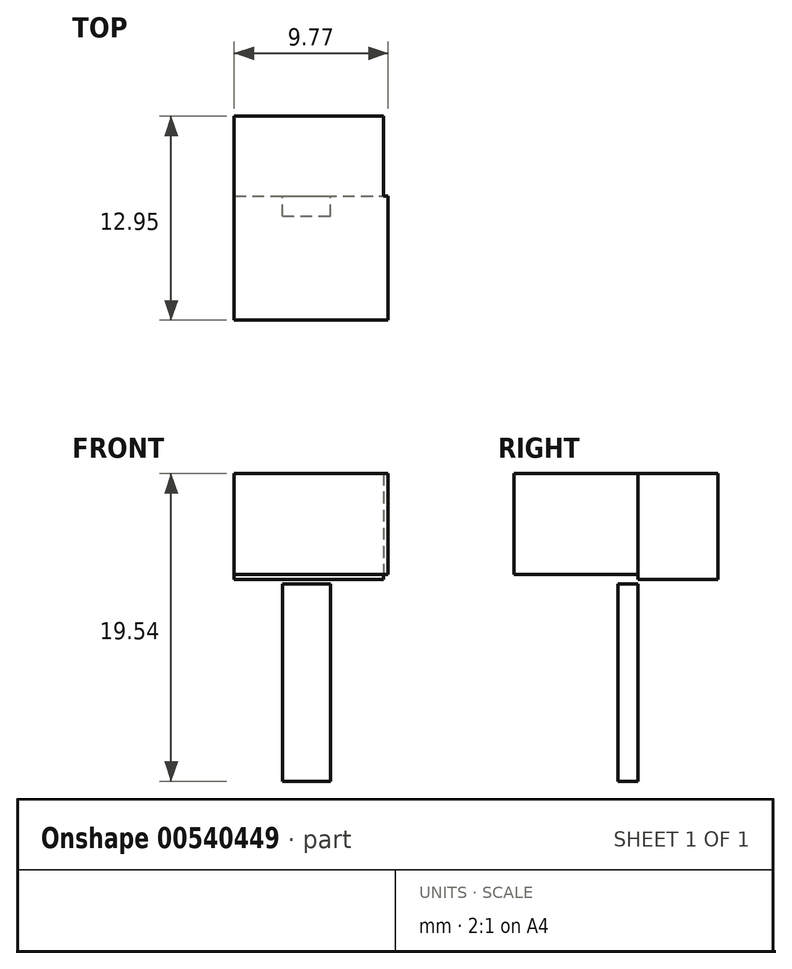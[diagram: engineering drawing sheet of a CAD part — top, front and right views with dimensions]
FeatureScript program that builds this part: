
annotation { "Feature Type Name" : "Feature", "Feature Type Description" : "" }
export const myFeature = defineFeature(function(context is Context, id is Id, definition is map)
    precondition{}
    {
        {
            var Q0;
            Q0=qCreatedBy(makeId("Front.planeOp"),FACE);
            var sketch = newSketch(context, id + "F0", { "sketchPlane" : qUnion([Q0])});
            skLineSegment(sketch, "E0.bottom", {"start": v(-57.72, -44.9) * mm, "end": v(-54.66, -44.9) * mm});
            skLineSegment(sketch, "E0.top", {"start": v(-57.72, -32.37) * mm, "end": v(-54.66, -32.37) * mm});
            skLineSegment(sketch, "E0.left", {"start": v(-57.72, -44.9) * mm, "end": v(-57.72, -32.37) * mm});
            skLineSegment(sketch, "E0.right", {"start": v(-54.66, -44.9) * mm, "end": v(-54.66, -32.37) * mm});
            skSolve(sketch);
        }
        {
            var Q0;
            Q0 = qSketchRegion(id + "F0", true);
            extrude(context, id + "F1", {"entities" : qUnion([Q0]), "depth" : 1.27 * mm, "offsetDistance" : 25.4 * mm});
        }
        {
            var Q0;
            Q0=qCreatedBy(makeId("Front.planeOp"),FACE);
            var sketch = newSketch(context, id + "F2", { "sketchPlane" : qUnion([Q0])});
            skLineSegment(sketch, "E1.bottom", {"start": v(-60.77, -31.76) * mm, "end": v(-51, -31.76) * mm});
            skLineSegment(sketch, "E1.top", {"start": v(-60.77, -25.35) * mm, "end": v(-51, -25.35) * mm});
            skLineSegment(sketch, "E1.left", {"start": v(-60.77, -31.76) * mm, "end": v(-60.77, -25.35) * mm});
            skLineSegment(sketch, "E1.right", {"start": v(-51, -31.76) * mm, "end": v(-51, -25.35) * mm});
            skSolve(sketch);
        }
        {
            var Q0;
            Q0 = qSketchRegion(id + "F2", true);
            extrude(context, id + "F3", {"entities" : qUnion([Q0]), "depth" : 7.87 * mm, "offsetDistance" : 25.4 * mm});
        }
        {
            var Q0;
            Q0=qCreatedBy(makeId("Front.planeOp"),FACE);
            var sketch = newSketch(context, id + "F4", { "sketchPlane" : qUnion([Q0])});
            skLineSegment(sketch, "E2.bottom", {"start": v(-51.3, -25.35) * mm, "end": v(-60.77, -25.35) * mm});
            skLineSegment(sketch, "E2.top", {"start": v(-51.3, -32.07) * mm, "end": v(-60.77, -32.07) * mm});
            skLineSegment(sketch, "E2.left", {"start": v(-51.3, -25.35) * mm, "end": v(-51.3, -32.07) * mm});
            skLineSegment(sketch, "E2.right", {"start": v(-60.77, -25.35) * mm, "end": v(-60.77, -32.07) * mm});
            skSolve(sketch);
        }
        {
            var Q0;
            Q0 = qSketchRegion(id + "F4", true);
            extrude(context, id + "F5", {"entities" : qUnion([Q0]), "operationType" : NewBodyOperationType.ADD, "oppositeDirection" : true, "depth" : 5.08 * mm, "offsetDistance" : 25.4 * mm});
        }
    });
